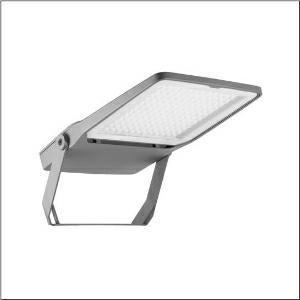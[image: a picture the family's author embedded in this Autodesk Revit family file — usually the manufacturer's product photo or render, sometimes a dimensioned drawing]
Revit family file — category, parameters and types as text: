
# Revit family: floodlight_fl_20_midi___pl52_5xa7682d2d1ac_9f95
name_source: partatom
category: Lighting Fixtures
units: mm (PartAtom-declared; Revit-internal decimal feet)

## family parameters
Cut with Voids When Loaded = No
Host = Face
Light Source = No
Part Type = Normal
Room Calculation Point = No
Round Connector Dimension = Use Diameter
Shared = No

## types (1)
- --- (1 x LED 4000K / CRI = 70 (unbekannt), 17990 lm, 4000K)
    Apparent Load = 142 VA
    CIE Flux Codes = 27 59 98 100 100
    Color Rendering = 70
    Color Temperature = 4000K
    Default Elevation = 1800 mm
    Description = Floodlight FL 20 midi, floodlight, primary light control with lens, of plastic, primary optical cover: protective disc, of toughened safety glass, transparent, light distribution: PL52, light emission: direct distribution, primary light characteristic: asymmetric, installation type: surface-mounted, LED High Power LED, rated luminous flux: 17.990 lm, light colour: 740, colour temperature: 4000K, control gear: ECG Plus, control: flexible luminous flux parameterisation, time-dependent luminous flux control, digital communication interface, power reduction, overheat protection, electronic power reduction, with terminal, 5-pole, max. 2.5mm², mains connection: 220..240V, AC, 50/60Hz, rated input power: 142W, LED unit, of diecast aluminium, powder-coated, Siteco® metallic grey (DB 702S), length: 654 mm, width: 450 mm, height: 76mm, housing frame, of diecast aluminium, powder-coated, Siteco® metallic grey (DB 702S), mounting bracket, of steel, powder-coated, Siteco® metallic grey (DB 702S), DALIprotection rating (complete): IP66, insulation class (complete): insulation class II (safety insulation), certification: CE, ENEC, VDE, protection symbol: D, permissible ambient temperature for indoor applications: -40..+40°C, permissible ambient temperature for outdoor applications: -40..+50°C, standard: DIN EN 12944, packaging unit: 1 piece

Light Distribution: PL52
    Height = 76 mm
    Lamp = 1 x LED 4000K / CRI >= 70 (unbekannt)
    Lamp Light Flux = 17990 lm
    Lamp count = 1
    Length = 672 mm
    Luminous efficacy = 127 lm/W
    Manufacturer = Siteco
    ModVariant = No
    Model = 5XA7682D2D1AC
    Number of Poles = 1
    OnlyDefault = Yes
    Power Factor = 1
    Product Name = Floodlight FL 20 midi | PL52
    Product group = floodlight | pylon top
    ProductGroupID = 6101
    Protection Class = Protection class II
    Protection Degree = IP 66
    RLX_Detail_Level = 1
    RlxData = <blob elided: 97865 chars, md5=3968a09e>
    Socket = socket
    Standby Power = 0 W
    System Light Flux = 17990 lm
    System Power = 142 W
    Type Comments = factory setting: luminous flux: 100 % | dim-lin: 254 | 489 mA
    Type Image = l_1005943.jpg
    URL = http://relux.com
    VarID = @adj_143295
    Voltage = 0 V
    Weight = 0.00 kg
    Width = 450 mm

## geometry (parser evidence)
native form markers: Blend x4, Sweep x10
no freeform markers — native parametric forms only
